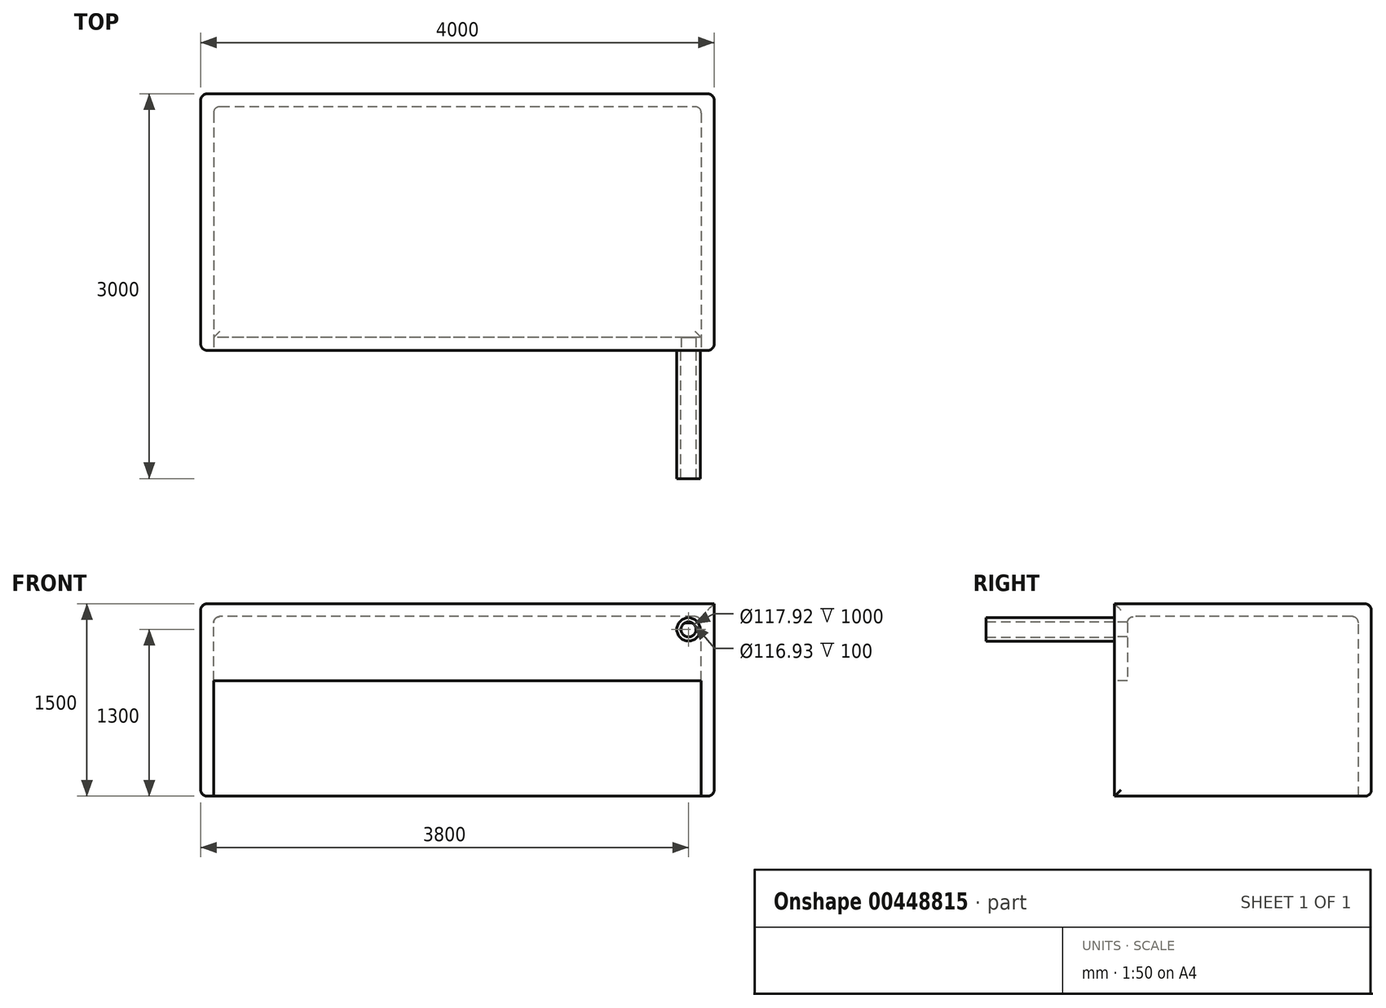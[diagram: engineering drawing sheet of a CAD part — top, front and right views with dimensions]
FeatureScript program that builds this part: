
annotation { "Feature Type Name" : "Feature", "Feature Type Description" : "" }
export const myFeature = defineFeature(function(context is Context, id is Id, definition is map)
    precondition{}
    {
        {
            var Q0;
            Q0=qCreatedBy(makeId("Top.planeOp"),FACE);
            var sketch = newSketch(context, id + "F0", { "sketchPlane" : qUnion([Q0])});
            skLineSegment(sketch, "E0.bottom", {"start": v(-1979.06, 816.1) * mm, "end": v(2020.94, 816.1) * mm});
            skLineSegment(sketch, "E0.top", {"start": v(-1979.06, -1183.9) * mm, "end": v(2020.94, -1183.9) * mm});
            skLineSegment(sketch, "E0.left", {"start": v(-1979.06, 816.1) * mm, "end": v(-1979.06, -1183.9) * mm});
            skLineSegment(sketch, "E0.right", {"start": v(2020.94, 816.1) * mm, "end": v(2020.94, -1183.9) * mm});
            skSolve(sketch);
        }
        {
            var Q0;
            Q0 = qSketchRegion(id + "F0", true);
            extrude(context, id + "F1", {"entities" : qUnion([Q0]), "depth" : 1500 * mm});
        }
        {
            var Q0;
            Q0=makeQuery(id+"F1.opExtrude","SWEPT_FACE",FACE,{"disambiguationData":[OSD([sQuery(id+"F0.wireOp",EDGE,"E0.top")])]});
            var sketch = newSketch(context, id + "F2", { "sketchPlane" : qUnion([Q0])});
            skLineSegment(sketch, "E1.bottom", {"start": v(1920.94, 0) * mm, "end": v(-1879.06, 0) * mm});
            skLineSegment(sketch, "E1.top", {"start": v(1920.94, 900) * mm, "end": v(-1879.06, 900) * mm});
            skLineSegment(sketch, "E1.left", {"start": v(1920.94, 0) * mm, "end": v(1920.94, 900) * mm});
            skLineSegment(sketch, "E1.right", {"start": v(-1879.06, 0) * mm, "end": v(-1879.06, 900) * mm});
            skSolve(sketch);
        }
        {
            var Q0;
            Q0 = qSketchRegion(id + "F2", true);
            extrude(context, id + "F3", {"entities" : qUnion([Q0]), "operationType" : NewBodyOperationType.REMOVE, "oppositeDirection" : true, "depth" : 1900 * mm});
        }
        {
            var Q0;
            Q0=makeQuery(id+"F3.boolean.opBoolean","COPY",FACE,{"derivedFrom":makeQuery(id+"F3.opExtrude","SWEPT_FACE",FACE,{"disambiguationData":[OSD([sQuery(id+"F2.wireOp",EDGE,"E1.top")])]})});
            var sketch = newSketch(context, id + "F4", { "sketchPlane" : qUnion([Q0])});
            skLineSegment(sketch, "E2.bottom", {"start": v(1920.94, -716.1) * mm, "end": v(-1879.06, -716.1) * mm});
            skLineSegment(sketch, "E2.top", {"start": v(1920.94, 1083.9) * mm, "end": v(-1879.06, 1083.9) * mm});
            skLineSegment(sketch, "E2.left", {"start": v(1920.94, -716.1) * mm, "end": v(1920.94, 1083.9) * mm});
            skLineSegment(sketch, "E2.right", {"start": v(-1879.06, -716.1) * mm, "end": v(-1879.06, 1083.9) * mm});
            skSolve(sketch);
        }
        {
            var Q0;
            Q0 = qSketchRegion(id + "F4", true);
            extrude(context, id + "F5", {"entities" : qUnion([Q0]), "operationType" : NewBodyOperationType.REMOVE, "oppositeDirection" : true, "depth" : 500 * mm});
        }
        {
            var Q0;
            Q0=makeQuery(id+"F1.opExtrude","SWEPT_FACE",FACE,{"disambiguationData":[OSD([sQuery(id+"F0.wireOp",EDGE,"E0.top")])]});
            var sketch = newSketch(context, id + "F6", { "sketchPlane" : qUnion([Q0])});
            skCircle(sketch, "E3", {"center": v(1820.94, 1300) * mm, "radius": 90.72 * mm});
            skCircle(sketch, "E4", {"center": v(1820.94, 1300) * mm, "radius": 58.96 * mm});
            skSolve(sketch);
        }
        {
            var Q0;
            Q0 = qSketchRegion(id + "F6", true);
            extrude(context, id + "F7", {"entities" : qUnion([Q0]), "operationType" : NewBodyOperationType.ADD, "depth" : 1000 * mm});
        }
        {
            var Q0;
            Q0=makeQuery(id+"F3.boolean.opBoolean","COPY",EDGE,{"derivedFrom":makeQuery(id+"F3.opExtrude","CAP_EDGE",EDGE,{"disambiguationData":[OSD([sQuery(id+"F2.wireOp",EDGE,"E1.top")])],"isStart":true})});
            var Q1;
            Q1=makeQuery(id+"F1.opExtrude","SWEPT_EDGE",EDGE,{"disambiguationData":[OSD([sQuery(id+"F0.wireOp",EDGE,"E0.top"),sQuery(id+"F0.wireOp",EDGE,"E0.left")])]});
            var Q2;
            Q2=makeQuery(id+"F1.opExtrude","SWEPT_EDGE",EDGE,{"disambiguationData":[OSD([sQuery(id+"F0.wireOp",EDGE,"E0.top"),sQuery(id+"F0.wireOp",EDGE,"E0.right")])]});
            var Q3;
            Q3=makeQuery(id+"F1.opExtrude","SWEPT_EDGE",EDGE,{"disambiguationData":[OSD([sQuery(id+"F0.wireOp",EDGE,"E0.bottom"),sQuery(id+"F0.wireOp",EDGE,"E0.right")])]});
            var Q4;
            Q4=makeQuery(id+"F1.opExtrude","SWEPT_EDGE",EDGE,{"disambiguationData":[OSD([sQuery(id+"F0.wireOp",EDGE,"E0.bottom"),sQuery(id+"F0.wireOp",EDGE,"E0.left")])]});
            var Q5;
            Q5=makeQuery(id+"F5.boolean.opBoolean","COPY",EDGE,{"derivedFrom":makeQuery(id+"F5.opExtrude","CAP_EDGE",EDGE,{"disambiguationData":[OSD([sQuery(id+"F4.wireOp",EDGE,"E2.top")])],"isStart":true})});
            var Q6;
            Q6=makeQuery(id+"F1.opExtrude","CAP_EDGE",EDGE,{"disambiguationData":[OSD([sQuery(id+"F0.wireOp",EDGE,"E0.bottom")])],"isStart":true});
            var Q7;
            Q7=makeQuery(id+"F1.opExtrude","SWEPT_FACE",FACE,{"disambiguationData":[OSD([sQuery(id+"F0.wireOp",EDGE,"E0.left")])]});
            var Q8;
            Q8=makeQuery(id+"F3.boolean.opBoolean","COPY",EDGE,{"derivedFrom":makeQuery(id+"F3.opExtrude","SWEPT_EDGE",EDGE,{"disambiguationData":[OSD([sQuery(id+"F0.wireOp",EDGE,"E0.top"),sQuery(id+"F2.wireOp",EDGE,"E1.bottom"),sQuery(id+"F2.wireOp",EDGE,"E1.right")])]})});
            var Q9;
            Q9=makeQuery(id+"F3.boolean.opBoolean","COPY",EDGE,{"derivedFrom":makeQuery(id+"F3.opExtrude","SWEPT_EDGE",EDGE,{"disambiguationData":[OSD([sQuery(id+"F0.wireOp",EDGE,"E0.top"),sQuery(id+"F2.wireOp",EDGE,"E1.bottom"),sQuery(id+"F2.wireOp",EDGE,"E1.left")])]})});
            var Q10;
            Q10=makeQuery(id+"F1.opExtrude","CAP_EDGE",EDGE,{"disambiguationData":[OSD([sQuery(id+"F0.wireOp",EDGE,"E0.right")])],"isStart":true});
            var Q11;
            Q11=makeQuery(id+"F3.boolean.opBoolean","COPY",EDGE,{"derivedFrom":makeQuery(id+"F3.opExtrude","CAP_EDGE",EDGE,{"disambiguationData":[OSD([sQuery(id+"F2.wireOp",EDGE,"E1.left")])],"isStart":true})});
            var Q12;
            Q12=makeQuery(id+"F3.boolean.opBoolean","COPY",EDGE,{"derivedFrom":makeQuery(id+"F3.opExtrude","CAP_EDGE",EDGE,{"disambiguationData":[OSD([sQuery(id+"F2.wireOp",EDGE,"E1.right")])],"isStart":true})});
            var Q13;
            Q13=makeQuery(id+"F5.boolean.opBoolean","COPY",EDGE,{"derivedFrom":makeQuery(id+"F5.opExtrude","CAP_EDGE",EDGE,{"disambiguationData":[OSD([sQuery(id+"F4.wireOp",EDGE,"E2.bottom")])],"isStart":false})});
            var Q14;
            Q14=makeQuery(id+"F5.boolean.opBoolean","COPY",EDGE,{"derivedFrom":makeQuery(id+"F5.opExtrude","CAP_EDGE",EDGE,{"disambiguationData":[OSD([sQuery(id+"F4.wireOp",EDGE,"E2.right")])],"isStart":false})});
            var Q15;
            Q15=makeQuery(id+"F5.boolean.opBoolean","COPY",EDGE,{"derivedFrom":makeQuery(id+"F5.opExtrude","CAP_EDGE",EDGE,{"disambiguationData":[OSD([sQuery(id+"F4.wireOp",EDGE,"E2.left")])],"isStart":false})});
            var Q16;
            Q16=makeQuery(id+"F5.boolean.opBoolean","COPY",EDGE,{"derivedFrom":makeQuery(id+"F5.opExtrude","CAP_EDGE",EDGE,{"disambiguationData":[OSD([sQuery(id+"F4.wireOp",EDGE,"E2.top")])],"isStart":false})});
            var Q17;
            Q17=makeQuery(id+"F1.opExtrude","CAP_EDGE",EDGE,{"disambiguationData":[OSD([sQuery(id+"F0.wireOp",EDGE,"E0.bottom")])],"isStart":false});
            var Q18;
            Q18=makeQuery(id+"F5.boolean.opBoolean","MERGE",EDGE,{"derivedFrom":[makeQuery(id+"F3.boolean.opBoolean","COPY",EDGE,{"derivedFrom":makeQuery(id+"F3.opExtrude","CAP_EDGE",EDGE,{"disambiguationData":[OSD([sQuery(id+"F2.wireOp",EDGE,"E1.left")])],"isStart":false})}),makeQuery(id+"F5.opExtrude","SWEPT_EDGE",EDGE,{"disambiguationData":[OSD([sQuery(id+"F4.wireOp",EDGE,"E2.bottom"),sQuery(id+"F4.wireOp",EDGE,"E2.left")])]})]});
            var Q19;
            Q19=makeQuery(id+"F5.boolean.opBoolean","MERGE",EDGE,{"derivedFrom":[makeQuery(id+"F3.boolean.opBoolean","COPY",EDGE,{"derivedFrom":makeQuery(id+"F3.opExtrude","CAP_EDGE",EDGE,{"disambiguationData":[OSD([sQuery(id+"F2.wireOp",EDGE,"E1.right")])],"isStart":false})}),makeQuery(id+"F5.opExtrude","SWEPT_EDGE",EDGE,{"disambiguationData":[OSD([sQuery(id+"F4.wireOp",EDGE,"E2.bottom"),sQuery(id+"F4.wireOp",EDGE,"E2.right")])]})]});
            fillet(context, id + "F8", {"entities" : qUnion([Q0, Q1, Q2, Q3, Q4, Q5, Q6, Q7, Q8, Q9, Q10, Q11, Q12, Q13, Q14, Q15, Q16, Q17, Q18, Q19]), "radius" : 50 * mm, "tangentPropagation" : true, "allowEdgeOverflow" : false});
        }
        {
            var Q0;
            Q0=makeQuery(id+"F7.boolean.opBoolean","SPLIT",FACE,{"disambiguationData":[TD([makeQuery(id+"F7.opExtrude","SWEPT_FACE",FACE,{"disambiguationData":[OSD([sQuery(id+"F6.wireOp",EDGE,"E4")])]})])],"derivedFrom":makeQuery(id+"F1.opExtrude","SWEPT_FACE",FACE,{"disambiguationData":[OSD([sQuery(id+"F0.wireOp",EDGE,"E0.top")])]})});
            var sketch = newSketch(context, id + "F9", { "sketchPlane" : qUnion([Q0])});
            skCircle(sketch, "E5", {"center": v(1820.94, 1300) * mm, "radius": 58.47 * mm});
            skSolve(sketch);
        }
        {
            var Q0;
            Q0 = qSketchRegion(id + "F9", true);
            extrude(context, id + "F10", {"entities" : qUnion([Q0]), "operationType" : NewBodyOperationType.REMOVE, "oppositeDirection" : true, "depth" : 100 * mm, "offsetDistance" : 25 * mm});
        }
    });
